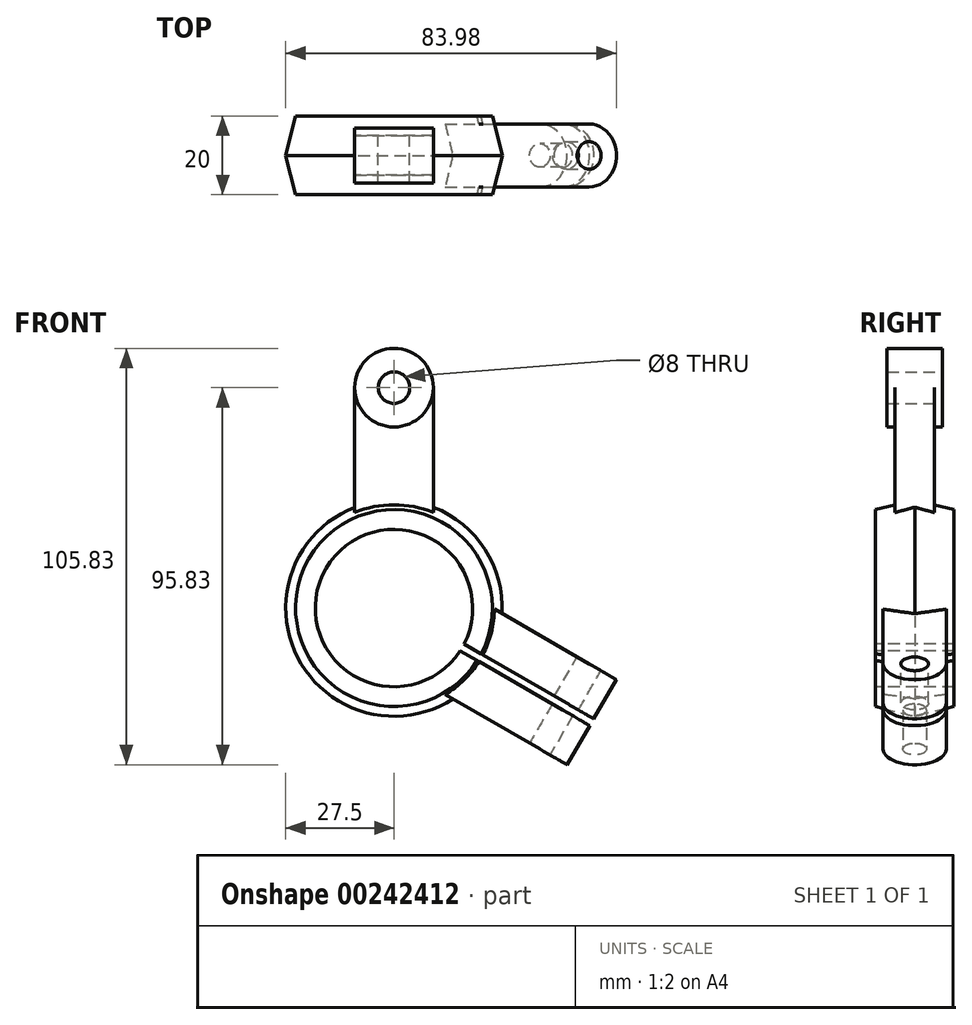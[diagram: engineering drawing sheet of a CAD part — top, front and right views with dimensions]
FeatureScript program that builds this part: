
annotation { "Feature Type Name" : "Feature", "Feature Type Description" : "" }
export const myFeature = defineFeature(function(context is Context, id is Id, definition is map)
    precondition{}
    {
        {
            var Q0;
            Q0=qCreatedBy(makeId("Front.planeOp"),FACE);
            var sketch = newSketch(context, id + "F0", { "sketchPlane" : qUnion([Q0])});
            skCircle(sketch, "E0", {"center": v(0, 0) * mm, "radius": 20 * mm});
            skCircle(sketch, "E1", {"center": v(0, 0) * mm, "radius": 25 * mm});
            skCircle(sketch, "E2", {"center": v(0, 0) * mm, "radius": 27.5 * mm});
            skLineSegment(sketch, "E3", {"start": v(0, 0) * mm, "end": v(0, 56) * mm});
            skCircle(sketch, "E4", {"center": v(0, 56) * mm, "radius": 10 * mm});
            skCircle(sketch, "E5", {"center": v(0, 56) * mm, "radius": 4 * mm});
            skLineSegment(sketch, "E6", {"start": v(-10, 56) * mm, "end": v(-10, 22.91) * mm});
            skLineSegment(sketch, "E7", {"start": v(10, 56) * mm, "end": v(10, 22.91) * mm});
            skLineSegment(sketch, "E8", {"start": v(-41.7, 0) * mm, "end": v(63.05, 0) * mm, "construction": true});
            skLineSegment(sketch, "E9", {"start": v(0, 0) * mm, "end": v(43.3, -25) * mm, "construction": true});
            skPoint(sketch, "E10", {"position": v(43.3, -25) * mm});
            skLineSegment(sketch, "E11", {"start": v(49.55, -14.17) * mm, "end": v(27.46, -1.42) * mm});
            skLineSegment(sketch, "E12", {"start": v(37.05, -35.83) * mm, "end": v(14.96, -23.07) * mm});
            skLineSegment(sketch, "E13", {"start": v(37.05, -35.83) * mm, "end": v(42.8, -25.87) * mm});
            skLineSegment(sketch, "E14", {"start": v(42.8, -25.87) * mm, "end": v(23.3, -14.6) * mm});
            skLineSegment(sketch, "E15.MirrorCS", {"start": v(43.8, -24.13) * mm, "end": v(24.3, -12.87) * mm});
            skLineSegment(sketch, "E16.MirrorCS", {"start": v(49.55, -14.17) * mm, "end": v(43.8, -24.13) * mm});
            skLineSegment(sketch, "E17", {"start": v(0, 0) * mm, "end": v(0, -49.76) * mm});
            skLineSegment(sketch, "E18", {"start": v(49.55, -14.17) * mm, "end": v(56.48, -18.17) * mm});
            skLineSegment(sketch, "E19", {"start": v(43.8, -24.13) * mm, "end": v(50.73, -28.13) * mm});
            skLineSegment(sketch, "E20", {"start": v(56.48, -18.17) * mm, "end": v(50.73, -28.13) * mm});
            skLineSegment(sketch, "E21.MirrorCS", {"start": v(42.8, -25.87) * mm, "end": v(49.73, -29.87) * mm});
            skLineSegment(sketch, "E22.MirrorCS", {"start": v(37.05, -35.83) * mm, "end": v(43.98, -39.83) * mm});
            skLineSegment(sketch, "E23.MirrorCS", {"start": v(43.98, -39.83) * mm, "end": v(49.73, -29.87) * mm});
            skLineSegment(sketch, "E24", {"start": v(14.96, -23.07) * mm, "end": v(12.5, -21.65) * mm});
            skLineSegment(sketch, "E25", {"start": v(23.3, -14.6) * mm, "end": v(21.13, -13.36) * mm});
            skLineSegment(sketch, "E26.MirrorCS", {"start": v(24.3, -12.87) * mm, "end": v(22.13, -11.62) * mm});
            skLineSegment(sketch, "E27.MirrorCS", {"start": v(27.46, -1.42) * mm, "end": v(25, 0) * mm});
            skSolve(sketch);
        }
        {
            var Q0;
            Q0=makeQuery(id+"F0.imprint","IMPRINT",FACE,{"disambiguationData":[TD([[makeQuery(id+"F0.imprint","IMPRINT",EDGE,{"derivedFrom":sQuery(id+"F0.wireOp",EDGE,"E5")}),-1.0]])]});
            extrude(context, id + "F1", {"entities" : qUnion([Q0]), "endBound" : BoundingType.SYMMETRIC, "depth" : 14 * mm});
        }
        {
            var Q0;
            Q0=qCreatedBy(makeId("Front.planeOp"),FACE);
            cPlane(context, id + "F2", {"entities" : qUnion([Q0]), "cplaneType" : CPlaneType.OFFSET, "offset" : 10 * mm, "width" : 150 * mm, "height" : 150 * mm});
        }
        {
            var Q0;
            Q0=qCreatedBy(id+"F2.planeOp",FACE);
            var sketch = newSketch(context, id + "F3", { "sketchPlane" : qUnion([Q0])});
            skCircle(sketch, "E28.0", {"center": v(0, 0) * mm, "radius": 25 * mm});
            skSolve(sketch);
        }
        {
            var Q0;
            Q0=qCreatedBy(makeId("Front.planeOp"),FACE);
            var sketch = newSketch(context, id + "F4", { "sketchPlane" : qUnion([Q0])});
            skCircle(sketch, "E29.0", {"center": v(0, 0) * mm, "radius": 27.5 * mm});
            skSolve(sketch);
        }
        {
            var Q0;
            Q0=makeQuery(id+"F4.imprint","IMPRINT",FACE,{"disambiguationData":[TD([[makeQuery(id+"F4.imprint","IMPRINT",EDGE,{"derivedFrom":sQuery(id+"F4.wireOp",EDGE,"E29.0")}),1.0]])]});
            var Q1;
            Q1=makeQuery(id+"F3.imprint","IMPRINT",FACE,{"disambiguationData":[TD([[makeQuery(id+"F3.imprint","IMPRINT",EDGE,{"derivedFrom":sQuery(id+"F3.wireOp",EDGE,"E28.0")}),1.0]])]});
            loft(context, id + "F5", {"sheetProfilesArray" : [{ "sheetProfileEntities" : qUnion([Q0]) }, { "sheetProfileEntities" : qUnion([Q1]) }]});
        }
        {
            var Q0;
            Q0=qCreatedBy(makeId("Front.planeOp"),FACE);
            cPlane(context, id + "F6", {"entities" : qUnion([Q0]), "cplaneType" : CPlaneType.OFFSET, "offset" : 10 * mm, "oppositeDirection" : true, "width" : 150 * mm, "height" : 150 * mm});
        }
        {
            var Q0;
            Q0=qCreatedBy(id+"F6.planeOp",FACE);
            var sketch = newSketch(context, id + "F7", { "sketchPlane" : qUnion([Q0])});
            skCircle(sketch, "E30.0", {"center": v(0, 0) * mm, "radius": 25 * mm});
            skSolve(sketch);
        }
        {
            var Q1;
            Q1=makeQuery(id+"F4.imprint","IMPRINT",FACE,{"disambiguationData":[TD([[makeQuery(id+"F4.imprint","IMPRINT",EDGE,{"derivedFrom":sQuery(id+"F4.wireOp",EDGE,"E29.0")}),1.0]])]});
            var Q2;
            Q2=makeQuery(id+"F7.imprint","IMPRINT",FACE,{"disambiguationData":[TD([[makeQuery(id+"F7.imprint","IMPRINT",EDGE,{"derivedFrom":sQuery(id+"F7.wireOp",EDGE,"E30.0")}),1.0]])]});
            loft(context, id + "F8", {"operationType" : NewBodyOperationType.ADD, "sheetProfilesArray" : [{ "sheetProfileEntities" : qUnion([Q1]) }, { "sheetProfileEntities" : qUnion([Q2]) }]});
        }
        {
            var Q0;
            {var subQ0=sQuery(id+"F0.wireOp",EDGE,"E7");var subQ1=sQuery(id+"F0.wireOp",EDGE,"E2");var subQ2=makeQuery(id+"F0.imprint","INTERSECT",VERTEX,{"derivedFrom":[subQ1,subQ0]});Q0=makeQuery(id+"F0.imprint","IMPRINT",FACE,{"disambiguationData":[TD([[makeQuery(id+"F0.imprint","IMPRINT",EDGE,{"disambiguationData":[TD([[subQ2,-1.0]])],"derivedFrom":subQ1}),-1.0]])]});}
            var Q1;
            {var subQ0=sQuery(id+"F0.wireOp",EDGE,"E6");var subQ1=sQuery(id+"F0.wireOp",EDGE,"E2");var subQ2=makeQuery(id+"F0.imprint","INTERSECT",VERTEX,{"derivedFrom":[subQ1,subQ0]});Q1=makeQuery(id+"F0.imprint","IMPRINT",FACE,{"disambiguationData":[TD([[makeQuery(id+"F0.imprint","IMPRINT",EDGE,{"disambiguationData":[TD([[subQ2,1.0]])],"derivedFrom":subQ1}),-1.0]])]});}
            var Q2;
            {var subQ0=sQuery(id+"F0.wireOp",EDGE,"E6");var subQ1=sQuery(id+"F0.wireOp",EDGE,"E1");var subQ2=makeQuery(id+"F0.imprint","INTERSECT",VERTEX,{"derivedFrom":[subQ1,subQ0]});Q2=makeQuery(id+"F0.imprint","IMPRINT",FACE,{"disambiguationData":[TD([[makeQuery(id+"F0.imprint","IMPRINT",EDGE,{"disambiguationData":[TD([[subQ2,1.0]])],"derivedFrom":subQ1}),-1.0]])]});}
            var Q3;
            {var subQ0=sQuery(id+"F0.wireOp",EDGE,"E7");var subQ1=sQuery(id+"F0.wireOp",EDGE,"E1");var subQ2=makeQuery(id+"F0.imprint","INTERSECT",VERTEX,{"derivedFrom":[subQ1,subQ0]});Q3=makeQuery(id+"F0.imprint","IMPRINT",FACE,{"disambiguationData":[TD([[makeQuery(id+"F0.imprint","IMPRINT",EDGE,{"disambiguationData":[TD([[subQ2,-1.0]])],"derivedFrom":subQ1}),-1.0]])]});}
            extrude(context, id + "F9", {"entities" : qUnion([Q0, Q1, Q2, Q3]), "operationType" : NewBodyOperationType.ADD, "endBound" : BoundingType.SYMMETRIC, "depth" : 10 * mm});
        }
        {
            var Q0;
            {var subQ0=sQuery(id+"F0.wireOp",EDGE,"E3");var subQ1=sQuery(id+"F0.wireOp",EDGE,"E0");var subQ2=makeQuery(id+"F0.imprint","INTERSECT",VERTEX,{"derivedFrom":[subQ1,subQ0]});Q0=makeQuery(id+"F0.imprint","IMPRINT",FACE,{"disambiguationData":[TD([[makeQuery(id+"F0.imprint","IMPRINT",EDGE,{"disambiguationData":[TD([[subQ2,-1.0]])],"derivedFrom":subQ1}),1.0]])]});}
            var Q1;
            {var subQ0=sQuery(id+"F0.wireOp",EDGE,"E3");var subQ1=sQuery(id+"F0.wireOp",EDGE,"E0");var subQ2=makeQuery(id+"F0.imprint","INTERSECT",VERTEX,{"derivedFrom":[subQ1,subQ0]});Q1=makeQuery(id+"F0.imprint","IMPRINT",FACE,{"disambiguationData":[TD([[makeQuery(id+"F0.imprint","IMPRINT",EDGE,{"disambiguationData":[TD([[subQ2,1.0]])],"derivedFrom":subQ1}),1.0]])]});}
            extrude(context, id + "F10", {"entities" : qUnion([Q0, Q1]), "operationType" : NewBodyOperationType.REMOVE, "endBound" : BoundingType.SYMMETRIC, "oppositeDirection" : true, "depth" : 48.8 * mm});
        }
        {
            var Q0;
            {var subQ0=sQuery(id+"F0.wireOp",EDGE,"E11");Q0=makeQuery(id+"F0.imprint","IMPRINT",FACE,{"disambiguationData":[TD([[makeQuery(id+"F0.imprint","IMPRINT",EDGE,{"derivedFrom":subQ0}),1.0]])]});}
            var Q1;
            Q1=makeQuery(id+"F0.imprint","IMPRINT",FACE,{"disambiguationData":[TD([[makeQuery(id+"F0.imprint","IMPRINT",EDGE,{"derivedFrom":sQuery(id+"F0.wireOp",EDGE,"E16.MirrorCS")}),1.0]])]});
            var Q2;
            Q2=makeQuery(id+"F0.imprint","IMPRINT",FACE,{"disambiguationData":[TD([[makeQuery(id+"F0.imprint","IMPRINT",EDGE,{"derivedFrom":sQuery(id+"F0.wireOp",EDGE,"E13")}),-1.0]])]});
            var Q3;
            {var subQ0=sQuery(id+"F0.wireOp",EDGE,"E12");Q3=makeQuery(id+"F0.imprint","IMPRINT",FACE,{"disambiguationData":[TD([[makeQuery(id+"F0.imprint","IMPRINT",EDGE,{"derivedFrom":subQ0}),-1.0]])]});}
            var Q4;
            {var subQ0=sQuery(id+"F0.wireOp",EDGE,"E26.MirrorCS");Q4=makeQuery(id+"F0.imprint","IMPRINT",FACE,{"disambiguationData":[TD([[makeQuery(id+"F0.imprint","IMPRINT",EDGE,{"derivedFrom":subQ0}),-1.0]])]});}
            var Q5;
            {var subQ0=sQuery(id+"F0.wireOp",EDGE,"E24");Q5=makeQuery(id+"F0.imprint","IMPRINT",FACE,{"disambiguationData":[TD([[makeQuery(id+"F0.imprint","IMPRINT",EDGE,{"derivedFrom":subQ0}),-1.0]])]});}
            extrude(context, id + "F11", {"entities" : qUnion([Q0, Q1, Q2, Q3, Q4, Q5]), "operationType" : NewBodyOperationType.ADD, "endBound" : BoundingType.SYMMETRIC, "depth" : 16 * mm});
        }
        {
            var Q0;
            Q0=makeQuery(id+"F11.opExtrude","SWEPT_FACE",FACE,{"disambiguationData":[OSD([sQuery(id+"F0.wireOp",EDGE,"E11"),sQuery(id+"F0.wireOp",EDGE,"E18"),sQuery(id+"F0.wireOp",EDGE,"E27.MirrorCS")])]});
            var sketch = newSketch(context, id + "F12", { "sketchPlane" : qUnion([Q0])});
            skFitSpline(sketch, "E31.0.0", {"points": [v(24.5, 0) * mm, v(23.75, -2.67) * mm, v(23, -5.34) * mm, v(22.23, -8) * mm]});
            skLineSegment(sketch, "E31.0.1", {"start": v(22.23, -8) * mm, "end": v(58, -8) * mm});
            skLineSegment(sketch, "E31.0.2", {"start": v(58, -8) * mm, "end": v(58, 8) * mm});
            skLineSegment(sketch, "E31.0.3", {"start": v(58, 8) * mm, "end": v(22.23, 8) * mm});
            skFitSpline(sketch, "E31.0.4", {"points": [v(22.23, 8) * mm, v(23, 5.34) * mm, v(23.75, 2.67) * mm, v(24.5, 0) * mm]});
            skLineSegment(sketch, "E32", {"start": v(58, 0) * mm, "end": v(50, 0) * mm});
            skPoint(sketch, "E32.endSnap0", {"position": v(58, 0) * mm});
            skCircle(sketch, "E33", {"center": v(50, 0) * mm, "radius": 8 * mm});
            skCircle(sketch, "E34", {"center": v(50, 0) * mm, "radius": 3.5 * mm});
            skSolve(sketch);
        }
        {
            var Q0;
            Q0=makeQuery(id+"F11.opExtrude","SWEPT_FACE",FACE,{"disambiguationData":[OSD([sQuery(id+"F0.wireOp",EDGE,"E23.MirrorCS")])]});
            var sketch = newSketch(context, id + "F13", { "sketchPlane" : qUnion([Q0])});
            skLineSegment(sketch, "E35.0.0", {"start": v(8, 1) * mm, "end": v(8, 12.5) * mm});
            skLineSegment(sketch, "E35.0.1", {"start": v(8, 12.5) * mm, "end": v(-8, 12.5) * mm});
            skLineSegment(sketch, "E35.0.2", {"start": v(-8, 12.5) * mm, "end": v(-8, 1) * mm});
            skLineSegment(sketch, "E35.0.3", {"start": v(-8, 1) * mm, "end": v(8, 1) * mm});
            skLineSegment(sketch, "E36.0.0", {"start": v(8, -12.5) * mm, "end": v(8, -1) * mm});
            skLineSegment(sketch, "E36.0.1", {"start": v(8, -1) * mm, "end": v(-8, -1) * mm});
            skLineSegment(sketch, "E36.0.2", {"start": v(-8, -1) * mm, "end": v(-8, -12.5) * mm});
            skLineSegment(sketch, "E36.0.3", {"start": v(-8, -12.5) * mm, "end": v(8, -12.5) * mm});
            skLineSegment(sketch, "E37", {"start": v(8, 1) * mm, "end": v(16.36, 1) * mm});
            skLineSegment(sketch, "E38", {"start": v(16.36, 1) * mm, "end": v(16.36, -1) * mm});
            skLineSegment(sketch, "E39", {"start": v(16.36, -1) * mm, "end": v(8, -1) * mm});
            skLineSegment(sketch, "E40", {"start": v(-8, 1) * mm, "end": v(-11.99, 1) * mm});
            skLineSegment(sketch, "E41", {"start": v(-11.99, 1) * mm, "end": v(-11.99, -1) * mm});
            skLineSegment(sketch, "E42", {"start": v(-11.99, -1) * mm, "end": v(-8, -1) * mm});
            skSolve(sketch);
        }
        {
            var Q0;
            Q0=makeQuery(id+"F13.imprint","IMPRINT",FACE,{"disambiguationData":[TD([[makeQuery(id+"F13.imprint","IMPRINT",EDGE,{"derivedFrom":sQuery(id+"F13.wireOp",EDGE,"E35.0.3")}),-1.0]])]});
            extrude(context, id + "F14", {"entities" : qUnion([Q0]), "operationType" : NewBodyOperationType.REMOVE, "oppositeDirection" : true, "depth" : 48.7 * mm});
        }
        {
            var Q0;
            {var subQ0=sQuery(id+"F12.wireOp",EDGE,"E31.0.2");var subQ1=sQuery(id+"F12.wireOp",EDGE,"E31.0.1");var subQ2=makeQuery(id+"F12.imprint","INTERSECT",VERTEX,{"derivedFrom":[subQ1,subQ0]});Q0=makeQuery(id+"F12.imprint","IMPRINT",FACE,{"disambiguationData":[TD([[makeQuery(id+"F12.imprint","IMPRINT",EDGE,{"disambiguationData":[TD([[subQ2,-1.0]])],"derivedFrom":subQ1}),-1.0]])]});}
            var Q1;
            {var subQ0=sQuery(id+"F12.wireOp",EDGE,"E31.0.3");var subQ1=sQuery(id+"F12.wireOp",EDGE,"E31.0.2");var subQ2=makeQuery(id+"F12.imprint","INTERSECT",VERTEX,{"derivedFrom":[subQ1,subQ0]});Q1=makeQuery(id+"F12.imprint","IMPRINT",FACE,{"disambiguationData":[TD([[makeQuery(id+"F12.imprint","IMPRINT",EDGE,{"disambiguationData":[TD([[subQ2,1.0]])],"derivedFrom":subQ1}),1.0]])]});}
            extrude(context, id + "F15", {"entities" : qUnion([Q0, Q1]), "operationType" : NewBodyOperationType.REMOVE, "endBound" : BoundingType.THROUGH_ALL, "oppositeDirection" : true, "depth" : 25 * mm});
        }
        {
            var Q0;
            Q0=makeQuery(id+"F12.imprint","IMPRINT",FACE,{"disambiguationData":[TD([[makeQuery(id+"F12.imprint","IMPRINT",EDGE,{"derivedFrom":sQuery(id+"F12.wireOp",EDGE,"E34")}),1.0]])]});
            extrude(context, id + "F16", {"entities" : qUnion([Q0]), "operationType" : NewBodyOperationType.REMOVE, "oppositeDirection" : true, "depth" : 12 * mm});
        }
        {
            var Q0;
            Q0=makeQuery(id+"F11.opExtrude","SWEPT_FACE",FACE,{"disambiguationData":[OSD([sQuery(id+"F0.wireOp",EDGE,"E12"),sQuery(id+"F0.wireOp",EDGE,"E22.MirrorCS"),sQuery(id+"F0.wireOp",EDGE,"E24")])]});
            var sketch = newSketch(context, id + "F17", { "sketchPlane" : qUnion([Q0])});
            skLineSegment(sketch, "E43.0", {"start": v(58, 0) * mm, "end": v(50, 0) * mm});
            skCircle(sketch, "E44", {"center": v(50, 0) * mm, "radius": 3 * mm});
            skSolve(sketch);
        }
        {
            var Q0;
            Q0=makeQuery(id+"F17.imprint","IMPRINT",FACE,{"disambiguationData":[TD([[makeQuery(id+"F17.imprint","IMPRINT",EDGE,{"derivedFrom":sQuery(id+"F17.wireOp",EDGE,"E44")}),1.0]])]});
            extrude(context, id + "F18", {"entities" : qUnion([Q0]), "operationType" : NewBodyOperationType.REMOVE, "oppositeDirection" : true, "depth" : 12 * mm});
        }
    });
